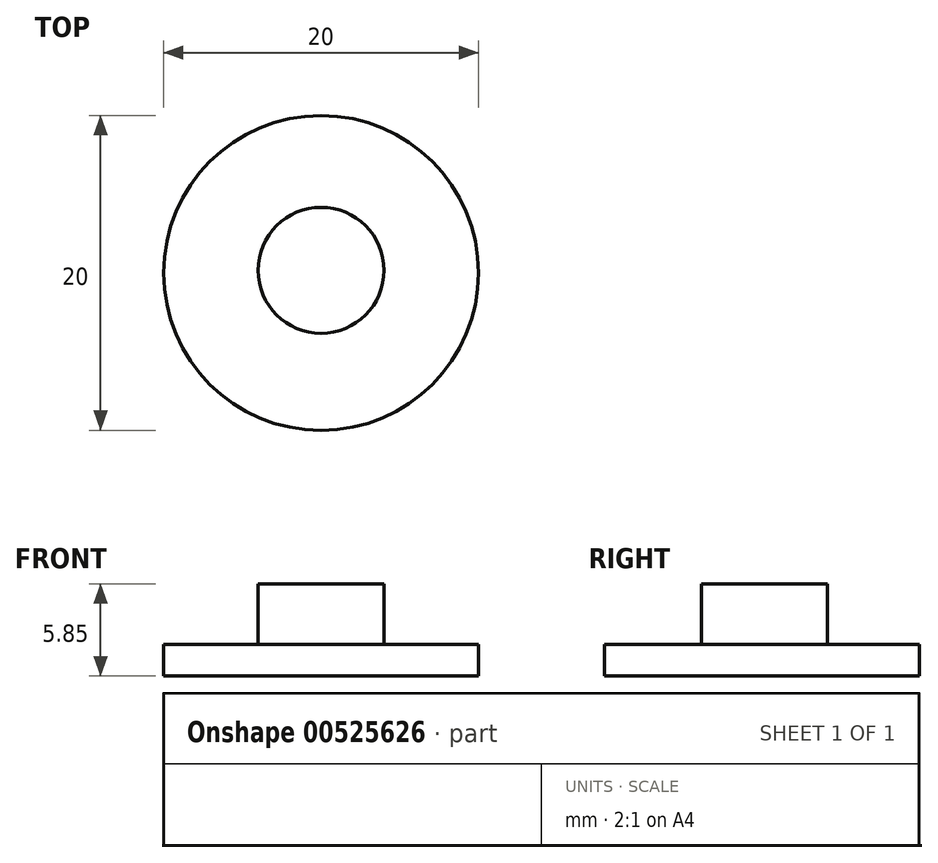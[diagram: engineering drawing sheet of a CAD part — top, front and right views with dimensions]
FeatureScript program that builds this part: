
annotation { "Feature Type Name" : "Feature", "Feature Type Description" : "" }
export const myFeature = defineFeature(function(context is Context, id is Id, definition is map)
    precondition{}
    {
        {
            var Q0;
            Q0=qCreatedBy(makeId("Top.planeOp"),FACE);
            var sketch = newSketch(context, id + "F0", { "sketchPlane" : qUnion([Q0])});
            skCircle(sketch, "E0", {"center": v(0, 0) * mm, "radius": 10 * mm});
            skCircle(sketch, "E1", {"center": v(0, 0) * mm, "radius": 4 * mm});
            skSolve(sketch);
        }
        {
            var Q0;
            Q0=makeQuery(id+"F0.imprint","IMPRINT",FACE,{"disambiguationData":[TD([[makeQuery(id+"F0.imprint","IMPRINT",EDGE,{"derivedFrom":sQuery(id+"F0.wireOp",EDGE,"E0")}),1.0]])]});
            var Q1;
            Q1=makeQuery(id+"F0.imprint","IMPRINT",FACE,{"disambiguationData":[TD([[makeQuery(id+"F0.imprint","IMPRINT",EDGE,{"derivedFrom":sQuery(id+"F0.wireOp",EDGE,"E1")}),1.0]])]});
            extrude(context, id + "F1", {"entities" : qUnion([Q0, Q1]), "oppositeDirection" : true, "depth" : 2 * mm, "offsetDistance" : 25.4 * mm});
        }
        {
            var Q0;
            Q0=makeQuery(id+"F1.opExtrude","CAP_FACE",FACE,{"disambiguationData":[OSD([sQuery(id+"F0.wireOp",EDGE,"E0")])],"isStart":true});
            var sketch = newSketch(context, id + "F2", { "sketchPlane" : qUnion([Q0])});
            skCircle(sketch, "E2", {"center": v(0, 0.17) * mm, "radius": 4 * mm});
            skSolve(sketch);
        }
        {
            var Q0;
            Q0 = qSketchRegion(id + "F2", true);
            extrude(context, id + "F3", {"entities" : qUnion([Q0]), "operationType" : NewBodyOperationType.ADD, "depth" : 3.85 * mm, "offsetDistance" : 25.4 * mm});
        }
    });
